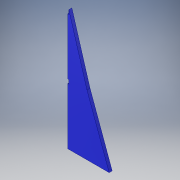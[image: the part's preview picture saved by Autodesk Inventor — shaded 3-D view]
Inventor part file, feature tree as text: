
AUTODESK INVENTOR PART (.ipt)
format: ipt  version: 2018 (Build 220112000, 112)  size: 111,616 bytes
history: native  units: in
note: dims shown in document units (in); Inventor stores cm internally (conversion verified against a paired STEP export)
features: extrude x1, sketch x1
ambient origin geometry x8: Origin, YZ Plane, XZ Plane, XY Plane, X Axis, Y Axis, Z Axis, Center Point
bodies: Solid1 (feature_tree)
feature tree (2):
  extrude  "Extrusion1"  Depth=0.5in
  sketch  "Sketch1"  dims[d0=15.0in d1=5.0in d2=7.5in d3=2.25in d4=0.375in d5=0.0in d7=0.125in d8=7.0in d9=0.125in d10=0.5in d11=0.5in]
